# Revit family: CORONADA_50_250_SX
name_source: partatom
category: Mechanical Equipment
revit_build: Autodesk Revit 2018 (Build: 20170223_1515(x64)
units: mm (PartAtom-declared; Revit-internal decimal feet)

## family parameters
Always vertical = Yes
Cut with Voids When Loaded = No
Part Type = Normal
Room Calculation Point = No
Round Connector Dimension = Use Radius
Shared = No
Work Plane-Based = No

## types (1)
- Coronada 250 SX
    Cable = PVC
    Cable Length (m) = 10 (with Schuko plug)
    Cable Type (H07RN-F) = 3G1.0
    Capacity(m3/hr) = 9 m³
    Description = Plug-in, stainless steel submersible pump, for the removal of
wastewater containing solids up to 10 mm.
    Discharge DN 32 = 16 mm  [stored 0.0524934 ft]
    Head(m) = 8 mm  [stored 0.0262467 ft]
    Impeller = PPO
    Manufacturer = Sulzer
    Model = Light Drainage Pump Type ABS Coronada 250
    Motor Housing = Stainless steel 1.4401 (AISI 316)
    Motor Power (kW) = P1=0.50 P2=0.30
    Motor Shaft = Stainless steel 1.4401 (AISI 316)
    Product Specification Link = https://www.sulzer.com
    Rated Current (A) = 2.28
    Rated Voltage (V) = 220-240 1~
    Seals = Viton

note: [stored X ft] marks values corroborated as IEEE doubles in the binary element streams (Revit-internal decimal feet)

## geometry (parser evidence)
native form markers: Sweep x3
no freeform markers — native parametric forms only
